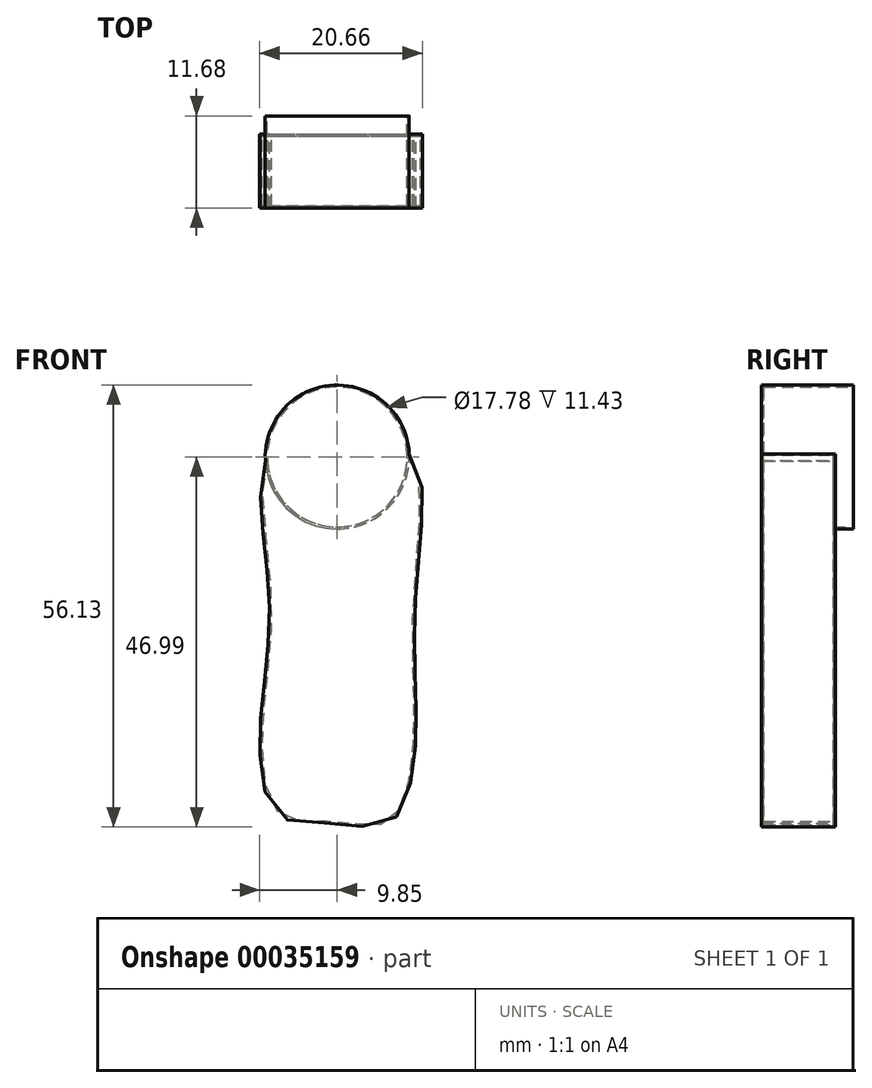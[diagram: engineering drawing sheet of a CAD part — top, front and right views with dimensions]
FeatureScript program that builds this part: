
annotation { "Feature Type Name" : "Feature", "Feature Type Description" : "" }
export const myFeature = defineFeature(function(context is Context, id is Id, definition is map)
    precondition{}
    {
        {
            var Q0;
            Q0=qCreatedBy(makeId("Front.planeOp"),FACE);
            var sketch = newSketch(context, id + "F0", { "sketchPlane" : qUnion([Q0])});
            skCircle(sketch, "E0", {"center": v(0, 0) * mm, "radius": 8.9 * mm});
            skSolve(sketch);
        }
        {
            var Q0;
            Q0=qCreatedBy(makeId("Front.planeOp"),FACE);
            var sketch = newSketch(context, id + "F1", { "sketchPlane" : qUnion([Q0])});
            skFitSpline(sketch, "E1", {"points": [v(0, 0) * mm, v(-8.52, 0) * mm, v(-8.42, -17.29) * mm, v(-9.53, -34.2) * mm, v(-7.32, -45.28) * mm, v(0, -46.29) * mm, v(6.64, -46.19) * mm, v(9.7, -36.32) * mm, v(9.7, -18.1) * mm, v(9.2, 0) * mm, v(0, 0) * mm]});
            skSolve(sketch);
        }
        {
            var Q0;
            Q0=makeQuery(id+"F1.imprint","IMPRINT",FACE,{"disambiguationData":[TD([[makeQuery(id+"F1.imprint","IMPRINT",EDGE,{"derivedFrom":sQuery(id+"F1.wireOp",EDGE,"E1")}),1.0]])]});
            extrude(context, id + "F2", {"entities" : qUnion([Q0]), "depth" : 8.9 * mm});
        }
        {
            var Q0;
            Q0=makeQuery(id+"F0.imprint","IMPRINT",FACE,{"disambiguationData":[TD([[makeQuery(id+"F0.imprint","IMPRINT",EDGE,{"derivedFrom":sQuery(id+"F0.wireOp",EDGE,"E0")}),1.0]])]});
            extrude(context, id + "F3", {"entities" : qUnion([Q0]), "operationType" : NewBodyOperationType.ADD, "depth" : 8.9 * mm, "hasSecondDirection" : true, "secondDirectionOppositeDirection" : true, "secondDirectionDepth" : 2.54 * mm});
        }
        {
            var Q0;
            Q0=makeQuery(id+"F3.opExtrude","CAP_FACE",FACE,{"disambiguationData":[OSD([sQuery(id+"F0.wireOp",EDGE,"E0")])],"isStart":true});
            shell(context, id + "F4", {"entities" : qUnion([Q0]), "thickness" : 0.25 * mm, "oppositeDirection" : true});
        }
    });
